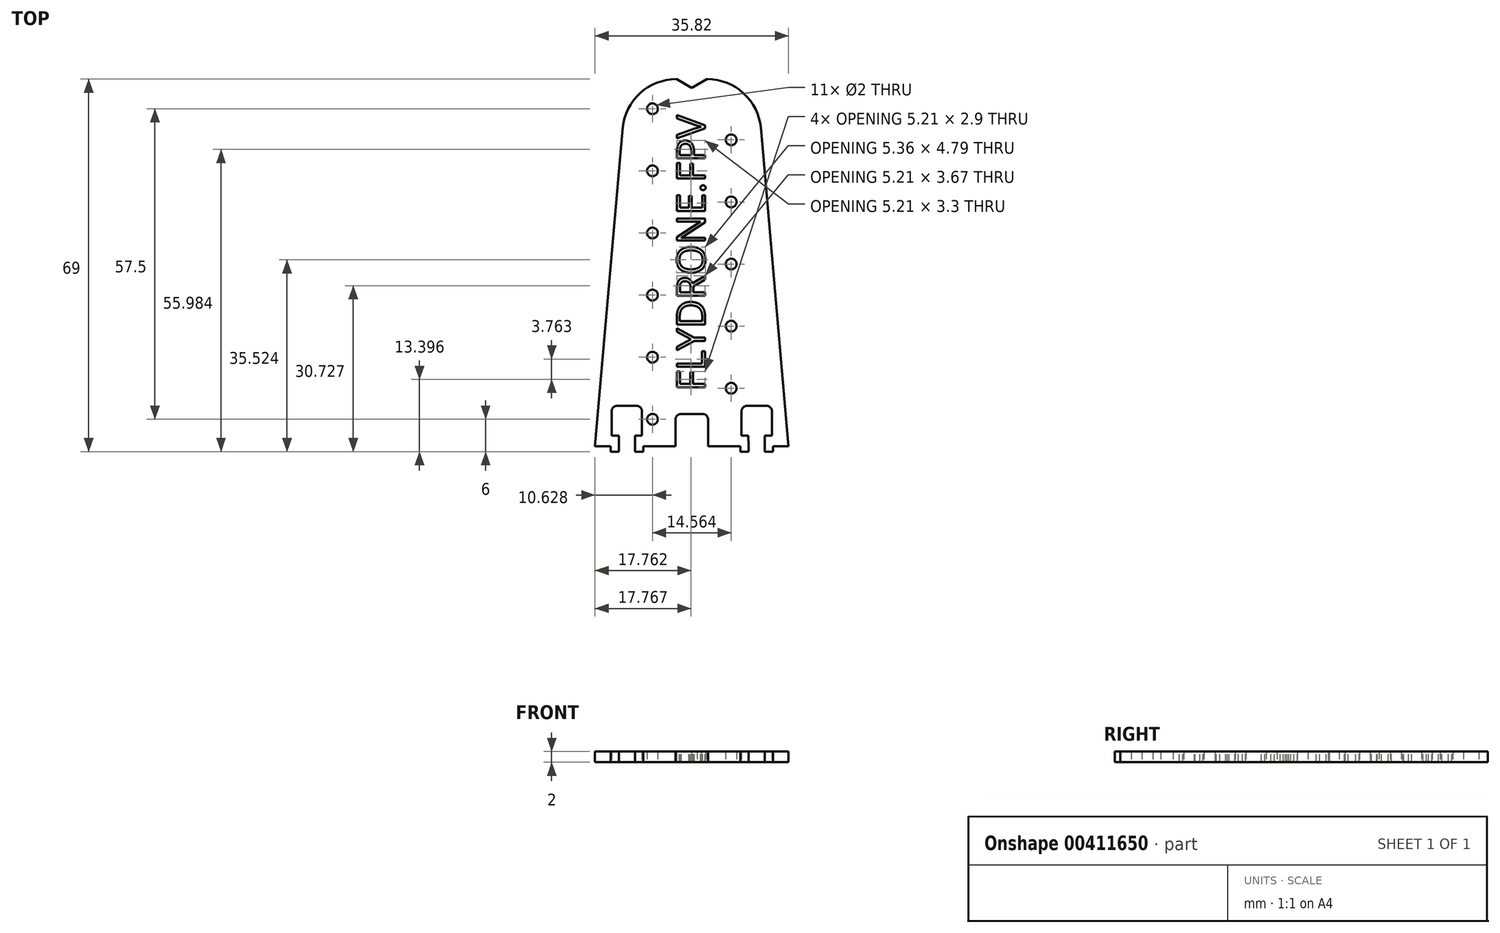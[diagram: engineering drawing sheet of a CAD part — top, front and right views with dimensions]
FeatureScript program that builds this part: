
annotation { "Feature Type Name" : "Feature", "Feature Type Description" : "" }
export const myFeature = defineFeature(function(context is Context, id is Id, definition is map)
    precondition{}
    {
        {
            var Q0;
            Q0=qCreatedBy(makeId("Top.planeOp"),FACE);
            var sketch = newSketch(context, id + "F0", { "sketchPlane" : qUnion([Q0])});
            skPoint(sketch, "E0.middle", {"position": v(0, 0) * mm});
            skLineSegment(sketch, "E1", {"start": v(12.8, 25.37) * mm, "end": v(17.91, -33.5) * mm});
            skLineSegment(sketch, "E2", {"start": v(-12.8, 25.37) * mm, "end": v(-17.91, -33.5) * mm});
            skPoint(sketch, "E3.visualSharp", {"position": v(-12, 34.5) * mm});
            skArc(sketch, "E3.filletArc", {"start": v(-2.83, 34.5) * mm, "mid": v(-9.59, 31.87) * mm, "end": v(-12.8, 25.37) * mm});
            skPoint(sketch, "E4.visualSharp", {"position": v(12, 34.5) * mm});
            skArc(sketch, "E4.filletArc", {"start": v(12.8, 25.37) * mm, "mid": v(9.59, 31.87) * mm, "end": v(2.83, 34.5) * mm});
            skLineSegment(sketch, "E5", {"start": v(13.5, -33.5) * mm, "end": v(13.5, -34.5) * mm});
            skLineSegment(sketch, "E6", {"start": v(15, -33.5) * mm, "end": v(15, -34.5) * mm});
            skLineSegment(sketch, "E7", {"start": v(10.5, -33.5) * mm, "end": v(10.5, -34.5) * mm});
            skLineSegment(sketch, "E8", {"start": v(9, -33.5) * mm, "end": v(9, -34.5) * mm});
            skLineSegment(sketch, "E9", {"start": v(3, -31.5) * mm, "end": v(3, -33.5) * mm});
            skLineSegment(sketch, "E10.trimOffspring", {"start": v(15, -33.5) * mm, "end": v(17.91, -33.5) * mm});
            skLineSegment(sketch, "E11.trimOffspring", {"start": v(13.5, -34.5) * mm, "end": v(15, -34.5) * mm});
            skLineSegment(sketch, "E12", {"start": v(13.5, -33.5) * mm, "end": v(13.5, -31.5) * mm});
            skLineSegment(sketch, "E13", {"start": v(10.5, -33.5) * mm, "end": v(10.47, -31.5) * mm});
            skLineSegment(sketch, "E14.trimOffspring", {"start": v(9, -34.5) * mm, "end": v(10.5, -34.5) * mm});
            skLineSegment(sketch, "E15", {"start": v(9.2, -31.5) * mm, "end": v(10.47, -31.5) * mm});
            skLineSegment(sketch, "E16", {"start": v(9.2, -31.5) * mm, "end": v(9.2, -27) * mm});
            skLineSegment(sketch, "E17", {"start": v(14.84, -31.5) * mm, "end": v(14.84, -27) * mm});
            skLineSegment(sketch, "E18.trimOffspring", {"start": v(13.5, -31.5) * mm, "end": v(14.84, -31.5) * mm});
            skLineSegment(sketch, "E19.trimOffspring", {"start": v(10.2, -26) * mm, "end": v(13.84, -26) * mm});
            skLineSegment(sketch, "E20", {"start": v(1, -27.5) * mm, "end": v(2, -27.5) * mm});
            skLineSegment(sketch, "E21", {"start": v(3, -31.5) * mm, "end": v(3, -28.5) * mm});
            skLineSegment(sketch, "E22", {"start": v(0, -49.92) * mm, "end": v(0, 44.74) * mm, "construction": true});
            skLineSegment(sketch, "E23.trimOffspring", {"start": v(3, -33.5) * mm, "end": v(9, -33.5) * mm});
            skLineSegment(sketch, "E24.MirrorCS", {"start": v(-1, -27.5) * mm, "end": v(-2, -27.5) * mm});
            skLineSegment(sketch, "E25.MirrorCS", {"start": v(-9.2, -31.5) * mm, "end": v(-10.47, -31.5) * mm});
            skLineSegment(sketch, "E26.MirrorCS", {"start": v(-13.5, -31.5) * mm, "end": v(-14.84, -31.5) * mm});
            skLineSegment(sketch, "E27.MirrorCS", {"start": v(-9, -33.5) * mm, "end": v(-9, -34.5) * mm});
            skLineSegment(sketch, "E28.MirrorCS", {"start": v(-10.5, -33.5) * mm, "end": v(-10.5, -34.5) * mm});
            skLineSegment(sketch, "E29.MirrorCS", {"start": v(-15, -33.5) * mm, "end": v(-15, -34.5) * mm});
            skLineSegment(sketch, "E30.MirrorCS", {"start": v(-13.5, -33.5) * mm, "end": v(-13.5, -34.5) * mm});
            skLineSegment(sketch, "E31.MirrorCS", {"start": v(-9.2, -31.5) * mm, "end": v(-9.2, -27) * mm});
            skLineSegment(sketch, "E32.MirrorCS", {"start": v(-3, -31.5) * mm, "end": v(-3, -33.5) * mm});
            skLineSegment(sketch, "E33.MirrorCS", {"start": v(-13.5, -34.5) * mm, "end": v(-15, -34.5) * mm});
            skLineSegment(sketch, "E34.MirrorCS", {"start": v(-10.5, -33.5) * mm, "end": v(-10.47, -31.5) * mm});
            skLineSegment(sketch, "E35.MirrorCS", {"start": v(-3, -31.5) * mm, "end": v(-3, -28.5) * mm});
            skLineSegment(sketch, "E36.MirrorCS", {"start": v(-14.84, -31.5) * mm, "end": v(-14.84, -27) * mm});
            skLineSegment(sketch, "E37.MirrorCS", {"start": v(-3, -33.5) * mm, "end": v(-9, -33.5) * mm});
            skLineSegment(sketch, "E38.MirrorCS", {"start": v(-10.2, -26) * mm, "end": v(-13.84, -26) * mm});
            skLineSegment(sketch, "E39.MirrorCS", {"start": v(-9, -34.5) * mm, "end": v(-10.5, -34.5) * mm});
            skLineSegment(sketch, "E40.MirrorCS", {"start": v(-13.5, -33.5) * mm, "end": v(-13.5, -31.5) * mm});
            skLineSegment(sketch, "E41.MirrorCS", {"start": v(-15, -33.5) * mm, "end": v(-17.91, -33.5) * mm});
            skPoint(sketch, "E42.visualSharp", {"position": v(-14.84, -26) * mm});
            skArc(sketch, "E42.filletArc", {"start": v(-13.84, -26) * mm, "mid": v(-14.55, -26.3) * mm, "end": v(-14.84, -27) * mm});
            skPoint(sketch, "E43.visualSharp", {"position": v(-9.2, -26) * mm});
            skArc(sketch, "E43.filletArc", {"start": v(-9.2, -27) * mm, "mid": v(-9.5, -26.3) * mm, "end": v(-10.2, -26) * mm});
            skPoint(sketch, "E44.visualSharp", {"position": v(9.2, -26) * mm});
            skArc(sketch, "E44.filletArc", {"start": v(10.2, -26) * mm, "mid": v(9.5, -26.3) * mm, "end": v(9.2, -27) * mm});
            skPoint(sketch, "E45.visualSharp", {"position": v(14.84, -26) * mm});
            skArc(sketch, "E45.filletArc", {"start": v(14.84, -27) * mm, "mid": v(14.55, -26.3) * mm, "end": v(13.84, -26) * mm});
            skPoint(sketch, "E46.visualSharp", {"position": v(-3, -27.5) * mm});
            skArc(sketch, "E46.filletArc", {"start": v(-2, -27.5) * mm, "mid": v(-2.7, -27.8) * mm, "end": v(-3, -28.5) * mm});
            skPoint(sketch, "E47.visualSharp", {"position": v(3, -27.5) * mm});
            skArc(sketch, "E47.filletArc", {"start": v(3, -28.5) * mm, "mid": v(2.7, -27.8) * mm, "end": v(2, -27.5) * mm});
            skCircle(sketch, "E48", {"center": v(-7.28, -28.5) * mm, "radius": 1 * mm});
            skCircle(sketch, "E49", {"center": v(-7.28, -17) * mm, "radius": 1 * mm});
            skCircle(sketch, "E50", {"center": v(-7.28, -5.5) * mm, "radius": 1 * mm});
            skCircle(sketch, "E51", {"center": v(-7.28, 6) * mm, "radius": 1 * mm});
            skCircle(sketch, "E52", {"center": v(-7.28, 17.5) * mm, "radius": 1 * mm});
            skCircle(sketch, "E53", {"center": v(-7.28, 29) * mm, "radius": 1 * mm});
            skPoint(sketch, "E54.middle", {"position": v(0, -27.5) * mm});
            skPoint(sketch, "E54.cornerSnap0", {"position": v(-1, -27.5) * mm});
            skPoint(sketch, "E54.bottom.end.orphan", {"position": v(1, -38.54) * mm});
            skPoint(sketch, "E55.orphan", {"position": v(-1, -38.54) * mm});
            skPoint(sketch, "E54.top.start.orphan", {"position": v(-1, -16.46) * mm});
            skPoint(sketch, "E56.orphan", {"position": v(1, -16.46) * mm});
            skPoint(sketch, "E57.visualSharp", {"position": v(-3.13, 25.4) * mm});
            skPoint(sketch, "E58.visualSharp", {"position": v(3.13, 25.4) * mm});
            skPoint(sketch, "E59.visualSharp", {"position": v(3.13, -25.4) * mm});
            skPoint(sketch, "E60.visualSharp", {"position": v(-3.13, -25.4) * mm});
            skLineSegment(sketch, "E61.top", {"start": v(0, 29.95) * mm, "end": v(1, 29.95) * mm});
            skPoint(sketch, "E62.visualSharp", {"position": v(-3.13, -23.33) * mm});
            skPoint(sketch, "E63.visualSharp", {"position": v(3.13, -23.33) * mm});
            skPoint(sketch, "E64.middle", {"position": v(0, 28.1) * mm});
            skPoint(sketch, "E65.orphan", {"position": v(-1, 31) * mm});
            skPoint(sketch, "E66.orphan", {"position": v(1, 31) * mm});
            skPoint(sketch, "E67.orphan", {"position": v(1.13, 29.95) * mm});
            skPoint(sketch, "E61.left.end.orphan", {"position": v(-1.13, 29.95) * mm});
            skPoint(sketch, "E68.orphan", {"position": v(-1, 25.18) * mm});
            skPoint(sketch, "E69.orphan", {"position": v(1, 25.18) * mm});
            skLineSegment(sketch, "E70", {"start": v(-2.83, 34.5) * mm, "end": v(0, 32.86) * mm});
            skLineSegment(sketch, "E71", {"start": v(0, 32.86) * mm, "end": v(2.83, 34.5) * mm});
            skPoint(sketch, "E72.start.orphan", {"position": v(0, 34.5) * mm});
            skLineSegment(sketch, "E73", {"start": v(-7.28, 46.44) * mm, "end": v(-7.28, -52.74) * mm, "construction": true});
            skLineSegment(sketch, "E74.MirrorCS", {"start": v(7.28, 46.44) * mm, "end": v(7.28, -52.74) * mm, "construction": true});
            skCircle(sketch, "E75", {"center": v(7.28, -22.75) * mm, "radius": 1 * mm});
            skCircle(sketch, "E76", {"center": v(7.28, -11.25) * mm, "radius": 1 * mm});
            skCircle(sketch, "E77", {"center": v(7.28, 0.25) * mm, "radius": 1 * mm});
            skCircle(sketch, "E78", {"center": v(7.28, 11.75) * mm, "radius": 1 * mm});
            skCircle(sketch, "E79", {"center": v(7.28, 23.25) * mm, "radius": 1 * mm});
            skPoint(sketch, "E80.MirrorCS.end.orphan", {"position": v(-3.13, 23.4) * mm});
            skPoint(sketch, "E80.MirrorCS.start.orphan", {"position": v(-3.13, -21.33) * mm});
            skPoint(sketch, "E81.MirrorCS.start.orphan", {"position": v(-1.13, -23.33) * mm});
            skPoint(sketch, "E82.end.orphan", {"position": v(1.13, -23.33) * mm});
            skPoint(sketch, "E82.start.orphan", {"position": v(1, -23.33) * mm});
            skPoint(sketch, "E83.MirrorCS.start.orphan", {"position": v(-1, -23.33) * mm});
            skPoint(sketch, "E54.right.end.orphan", {"position": v(1, -25.4) * mm});
            skPoint(sketch, "E84.right.start.orphan", {"position": v(3.13, -21.33) * mm});
            skPoint(sketch, "E58.filletArc.start.orphan", {"position": v(3.13, 23.4) * mm});
            skPoint(sketch, "E85.start.orphan", {"position": v(1.13, 25.4) * mm});
            skPoint(sketch, "E86.start.orphan", {"position": v(-1.13, 25.4) * mm});
            skLineSegment(sketch, "E87", {"start": v(-1, -27.5) * mm, "end": v(1, -27.5) * mm});
            skSolve(sketch);
        }
        {
            var Q0;
            Q0=makeQuery(id+"F0.imprint","IMPRINT",FACE,{"disambiguationData":[TD([[makeQuery(id+"F0.imprint","IMPRINT",EDGE,{"derivedFrom":sQuery(id+"F0.wireOp",EDGE,"E1")}),-1.0]])]});
            extrude(context, id + "F1", {"entities" : qUnion([Q0]), "depth" : 2 * mm});
        }
        {
            var Q0;
            Q0=makeQuery(id+"F1.opExtrude","CAP_FACE",FACE,{"disambiguationData":[OSD([sQuery(id+"F0.wireOp",EDGE,"E1"),sQuery(id+"F0.wireOp",EDGE,"E2"),sQuery(id+"F0.wireOp",EDGE,"E3.filletArc"),sQuery(id+"F0.wireOp",EDGE,"E4.filletArc"),sQuery(id+"F0.wireOp",EDGE,"E5"),sQuery(id+"F0.wireOp",EDGE,"E6"),sQuery(id+"F0.wireOp",EDGE,"E7"),sQuery(id+"F0.wireOp",EDGE,"E8"),sQuery(id+"F0.wireOp",EDGE,"E9"),sQuery(id+"F0.wireOp",EDGE,"E10.trimOffspring"),sQuery(id+"F0.wireOp",EDGE,"E11.trimOffspring"),sQuery(id+"F0.wireOp",EDGE,"E12"),sQuery(id+"F0.wireOp",EDGE,"E13"),sQuery(id+"F0.wireOp",EDGE,"E14.trimOffspring"),sQuery(id+"F0.wireOp",EDGE,"E16"),sQuery(id+"F0.wireOp",EDGE,"E17"),sQuery(id+"F0.wireOp",EDGE,"E18.trimOffspring"),sQuery(id+"F0.wireOp",EDGE,"E19.trimOffspring"),sQuery(id+"F0.wireOp",EDGE,"E20"),sQuery(id+"F0.wireOp",EDGE,"E21"),sQuery(id+"F0.wireOp",EDGE,"E15"),sQuery(id+"F0.wireOp",EDGE,"E23.trimOffspring"),sQuery(id+"F0.wireOp",EDGE,"E24.MirrorCS"),sQuery(id+"F0.wireOp",EDGE,"E25.MirrorCS"),sQuery(id+"F0.wireOp",EDGE,"E26.MirrorCS"),sQuery(id+"F0.wireOp",EDGE,"E27.MirrorCS"),sQuery(id+"F0.wireOp",EDGE,"E28.MirrorCS"),sQuery(id+"F0.wireOp",EDGE,"E29.MirrorCS"),sQuery(id+"F0.wireOp",EDGE,"E30.MirrorCS"),sQuery(id+"F0.wireOp",EDGE,"E31.MirrorCS"),sQuery(id+"F0.wireOp",EDGE,"E32.MirrorCS"),sQuery(id+"F0.wireOp",EDGE,"E33.MirrorCS"),sQuery(id+"F0.wireOp",EDGE,"E34.MirrorCS"),sQuery(id+"F0.wireOp",EDGE,"E35.MirrorCS"),sQuery(id+"F0.wireOp",EDGE,"E36.MirrorCS"),sQuery(id+"F0.wireOp",EDGE,"E37.MirrorCS"),sQuery(id+"F0.wireOp",EDGE,"E38.MirrorCS"),sQuery(id+"F0.wireOp",EDGE,"E39.MirrorCS"),sQuery(id+"F0.wireOp",EDGE,"E40.MirrorCS"),sQuery(id+"F0.wireOp",EDGE,"E41.MirrorCS"),sQuery(id+"F0.wireOp",EDGE,"E42.filletArc"),sQuery(id+"F0.wireOp",EDGE,"E43.filletArc"),sQuery(id+"F0.wireOp",EDGE,"E44.filletArc"),sQuery(id+"F0.wireOp",EDGE,"E45.filletArc"),sQuery(id+"F0.wireOp",EDGE,"E46.filletArc"),sQuery(id+"F0.wireOp",EDGE,"E47.filletArc"),sQuery(id+"F0.wireOp",EDGE,"E48"),sQuery(id+"F0.wireOp",EDGE,"E49"),sQuery(id+"F0.wireOp",EDGE,"E50"),sQuery(id+"F0.wireOp",EDGE,"E51"),sQuery(id+"F0.wireOp",EDGE,"E52"),sQuery(id+"F0.wireOp",EDGE,"E53"),sQuery(id+"F0.wireOp",EDGE,"E70"),sQuery(id+"F0.wireOp",EDGE,"E71"),sQuery(id+"F0.wireOp",EDGE,"E75"),sQuery(id+"F0.wireOp",EDGE,"E76"),sQuery(id+"F0.wireOp",EDGE,"E77"),sQuery(id+"F0.wireOp",EDGE,"E78"),sQuery(id+"F0.wireOp",EDGE,"E79"),sQuery(id+"F0.wireOp",EDGE,"E87")])],"isStart":false});
            var sketch = newSketch(context, id + "F2", { "sketchPlane" : qUnion([Q0])});
            skText(sketch, "E88", { "text": "FLYDRONE.FPV", "fontName": "OpenSans-Regular.ttf"});
            skPoint(sketch, "E88.secondSnap0", {"position": v(-15.35, -4.07) * mm});
            const initialGuessF2  = {"E88": [0.00246, -0.02327, 0, 1, 0.00525]};
            skSetInitialGuess(sketch, initialGuessF2);
            skSolve(sketch);
        }
        {
            var Q0;
            Q0 = qSketchRegion(id + "F2", true);
            extrude(context, id + "F3", {"entities" : qUnion([Q0]), "operationType" : NewBodyOperationType.REMOVE, "oppositeDirection" : true, "depth" : 25 * mm});
        }
    });
